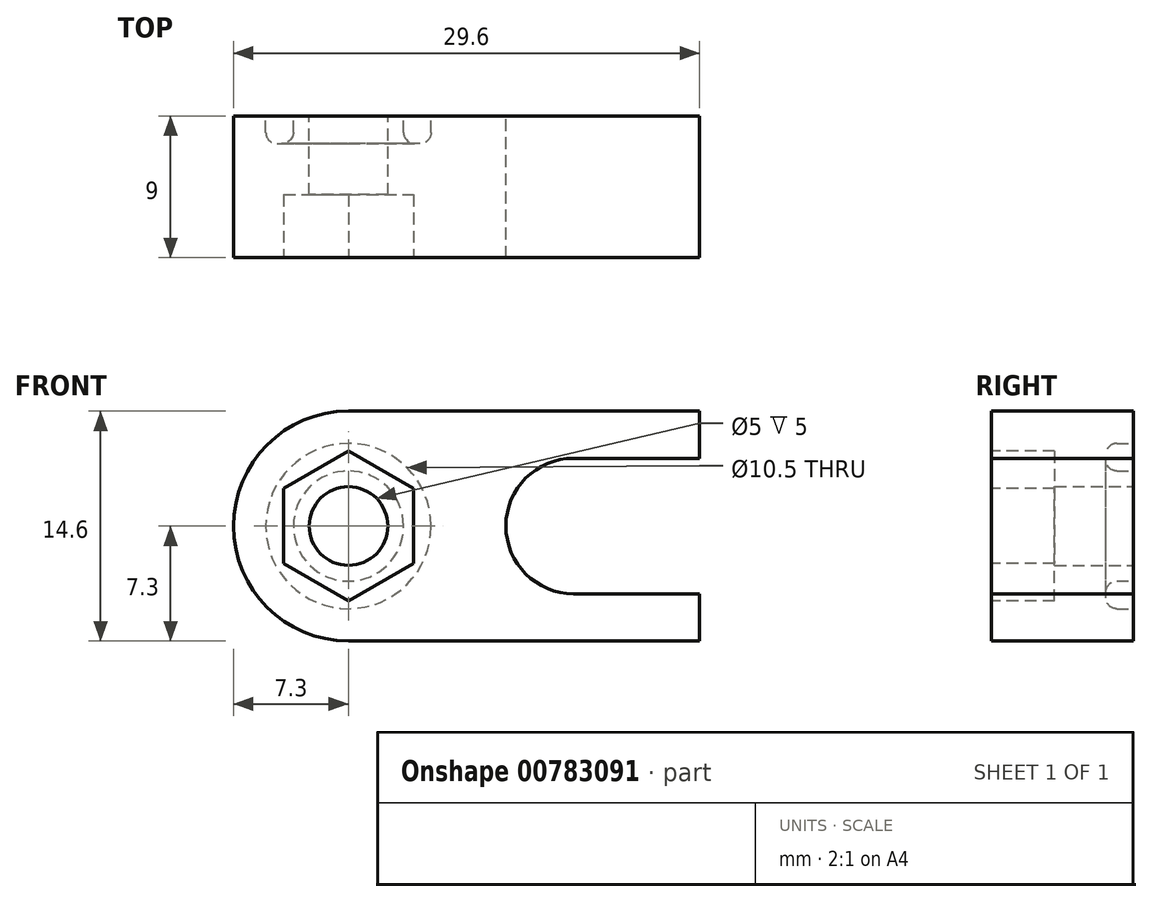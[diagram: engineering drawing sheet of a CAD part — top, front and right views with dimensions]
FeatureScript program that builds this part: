
annotation { "Feature Type Name" : "Feature", "Feature Type Description" : "" }
export const myFeature = defineFeature(function(context is Context, id is Id, definition is map)
    precondition{}
    {
        {
            var Q0;
            Q0=qCreatedBy(makeId("Front.planeOp"),FACE);
            var sketch = newSketch(context, id + "F0", { "sketchPlane" : qUnion([Q0])});
            skLineSegment(sketch, "E0.bottom", {"start": v(22.3, 7.3) * mm, "end": v(0, 7.3) * mm});
            skLineSegment(sketch, "E0.top", {"start": v(22.3, -7.3) * mm, "end": v(0, -7.3) * mm});
            skLineSegment(sketch, "E0.left", {"start": v(22.3, 7.3) * mm, "end": v(22.3, 4.3) * mm});
            skPoint(sketch, "E0.middle", {"position": v(0, 0) * mm});
            skArc(sketch, "E1", {"start": v(0, 7.3) * mm, "mid": v(-7.3, 0) * mm, "end": v(0, -7.3) * mm});
            skPoint(sketch, "E2.orphan", {"position": v(-22.3, 7.3) * mm});
            skPoint(sketch, "E3.orphan", {"position": v(-22.3, -7.3) * mm});
            skArc(sketch, "E4", {"start": v(14.3, 4.3) * mm, "mid": v(10, 0) * mm, "end": v(14.3, -4.3) * mm});
            skPoint(sketch, "E4.centerSnap0", {"position": v(22.3, 0) * mm});
            skLineSegment(sketch, "E5", {"start": v(14.3, 4.3) * mm, "end": v(22.3, 4.3) * mm});
            skLineSegment(sketch, "E6", {"start": v(14.3, -4.3) * mm, "end": v(22.3, -4.3) * mm});
            skLineSegment(sketch, "E7.trimOffspring", {"start": v(22.3, -4.3) * mm, "end": v(22.3, -7.3) * mm});
            skCircle(sketch, "E8", {"center": v(0, 0) * mm, "radius": 2.5 * mm});
            skSolve(sketch);
        }
        {
            var Q0;
            Q0=makeQuery(id+"F0.imprint","IMPRINT",FACE,{"disambiguationData":[TD([[makeQuery(id+"F0.imprint","IMPRINT",EDGE,{"derivedFrom":sQuery(id+"F0.wireOp",EDGE,"E0.bottom")}),1.0]])]});
            extrude(context, id + "F1", {"entities" : qUnion([Q0]), "depth" : 9 * mm, "offsetDistance" : 25 * mm});
        }
        {
            var Q0;
            Q0=makeQuery(id+"F1.opExtrude","CAP_FACE",FACE,{"disambiguationData":[OSD([sQuery(id+"F0.wireOp",EDGE,"E0.bottom"),sQuery(id+"F0.wireOp",EDGE,"E0.top"),sQuery(id+"F0.wireOp",EDGE,"E0.left"),sQuery(id+"F0.wireOp",EDGE,"E1"),sQuery(id+"F0.wireOp",EDGE,"E4"),sQuery(id+"F0.wireOp",EDGE,"E5"),sQuery(id+"F0.wireOp",EDGE,"E6"),sQuery(id+"F0.wireOp",EDGE,"E7.trimOffspring"),sQuery(id+"F0.wireOp",EDGE,"E8")])],"isStart":false});
            var sketch = newSketch(context, id + "F2", { "sketchPlane" : qUnion([Q0])});
            skCircle(sketch, "E9.cCircle", {"center": v(0, 0) * mm, "radius": 4.12 * mm, "construction": true});
            skLineSegment(sketch, "E9.0", {"start": v(4.12, 2.38) * mm, "end": v(4.12, -2.38) * mm});
            skLineSegment(sketch, "E9.1", {"start": v(4.12, -2.38) * mm, "end": v(0, -4.76) * mm});
            skLineSegment(sketch, "E9.2", {"start": v(0, -4.76) * mm, "end": v(-4.12, -2.38) * mm});
            skLineSegment(sketch, "E9.3", {"start": v(-4.12, -2.38) * mm, "end": v(-4.13, 2.38) * mm});
            skLineSegment(sketch, "E9.4", {"start": v(-4.13, 2.38) * mm, "end": v(0, 4.76) * mm});
            skLineSegment(sketch, "E9.5", {"start": v(0, 4.76) * mm, "end": v(4.12, 2.38) * mm});
            skPoint(sketch, "E9.0.midPoint", {"position": v(4.12, 0) * mm});
            skSolve(sketch);
        }
        {
            var Q0;
            Q0=makeQuery(id+"F2.imprint","IMPRINT",FACE,{"disambiguationData":[TD([[makeQuery(id+"F2.imprint","IMPRINT",EDGE,{"derivedFrom":sQuery(id+"F2.wireOp",EDGE,"E9.0")}),-1.0]])]});
            extrude(context, id + "F3", {"entities" : qUnion([Q0]), "operationType" : NewBodyOperationType.REMOVE, "oppositeDirection" : true, "depth" : 4 * mm, "offsetDistance" : 25 * mm});
        }
        {
            var Q0;
            Q0=qCreatedBy(makeId("Front.planeOp"),FACE);
            var sketch = newSketch(context, id + "F4", { "sketchPlane" : qUnion([Q0])});
            skCircle(sketch, "E10", {"center": v(0, 0) * mm, "radius": 5.25 * mm});
            skCircle(sketch, "E11", {"center": v(0, 0) * mm, "radius": 3.5 * mm});
            skSolve(sketch);
        }
        {
            var Q0;
            Q0=makeQuery(id+"F4.imprint","IMPRINT",FACE,{"disambiguationData":[TD([[makeQuery(id+"F4.imprint","IMPRINT",EDGE,{"derivedFrom":sQuery(id+"F4.wireOp",EDGE,"E10")}),1.0]])]});
            extrude(context, id + "F5", {"entities" : qUnion([Q0]), "operationType" : NewBodyOperationType.REMOVE, "depth" : 1.75 * mm, "offsetDistance" : 25 * mm});
        }
        {
            var Q0;
            Q0=makeQuery(id+"F5.boolean.opBoolean","COPY",FACE,{"derivedFrom":makeQuery(id+"F5.opExtrude","CAP_FACE",FACE,{"disambiguationData":[OSD([sQuery(id+"F4.wireOp",EDGE,"E10"),sQuery(id+"F4.wireOp",EDGE,"E11")])],"isStart":false})});
            fillet(context, id + "F6", {"entities" : qUnion([Q0]), "radius" : 0.7 * mm, "tangentPropagation" : true, "allowEdgeOverflow" : false});
        }
    });
